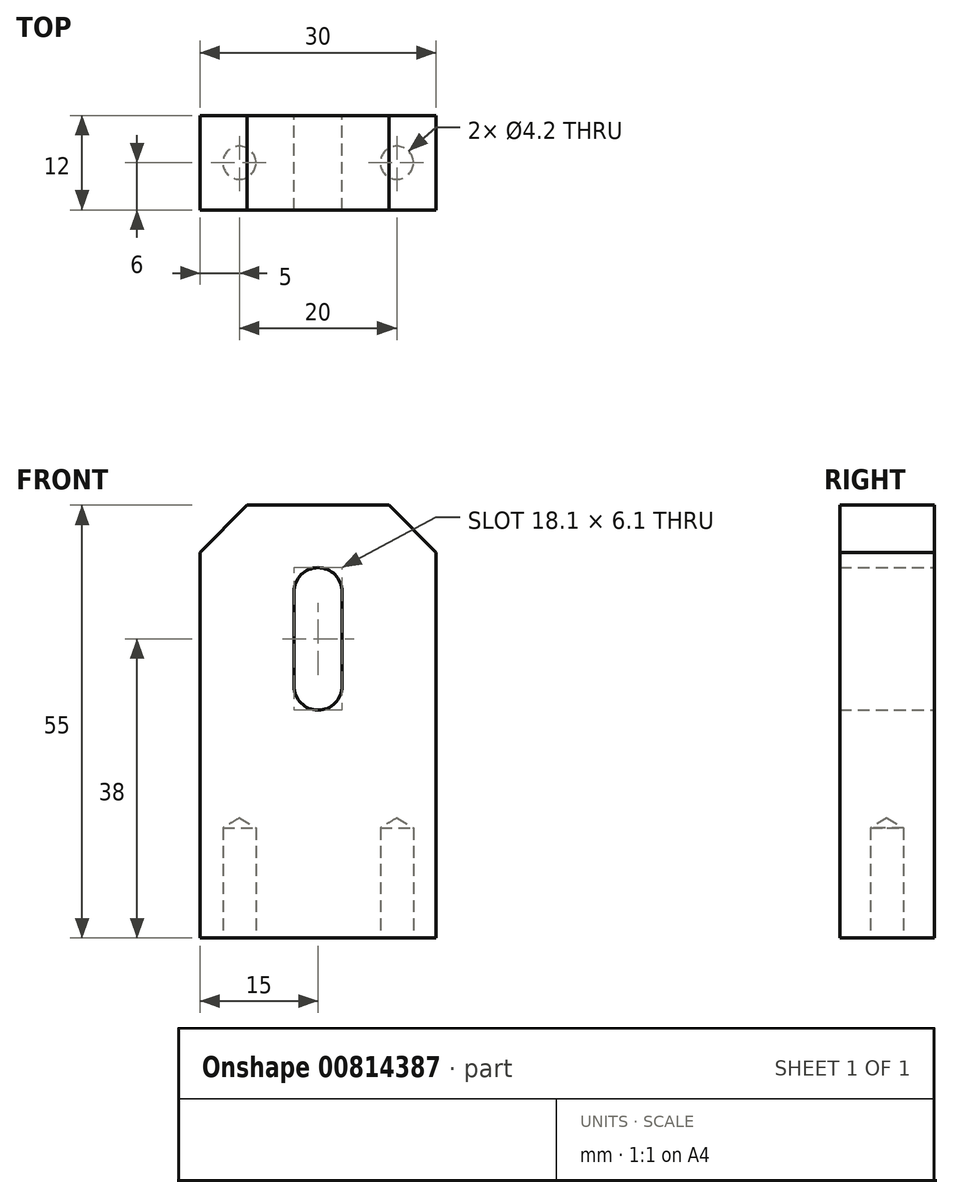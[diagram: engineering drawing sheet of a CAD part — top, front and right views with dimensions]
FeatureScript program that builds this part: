
annotation { "Feature Type Name" : "Feature", "Feature Type Description" : "" }
export const myFeature = defineFeature(function(context is Context, id is Id, definition is map)
    precondition{}
    {
        {
            var Q0;
            Q0=qCreatedBy(makeId("Front.planeOp"),FACE);
            var sketch = newSketch(context, id + "F0", { "sketchPlane" : qUnion([Q0])});
            skLineSegment(sketch, "E0.bottom", {"start": v(-15, -27.5) * mm, "end": v(15, -27.5) * mm});
            skLineSegment(sketch, "E0.top", {"start": v(-15, 27.5) * mm, "end": v(15, 27.5) * mm});
            skLineSegment(sketch, "E0.left", {"start": v(-15, -27.5) * mm, "end": v(-15, 27.5) * mm});
            skLineSegment(sketch, "E0.right", {"start": v(15, -27.5) * mm, "end": v(15, 27.5) * mm});
            skCircle(sketch, "E1", {"center": v(0, 16.5) * mm, "radius": 3.05 * mm});
            skPoint(sketch, "E2.center.orphan", {"position": v(0, 14.16) * mm});
            skCircle(sketch, "E3", {"center": v(0, 4.5) * mm, "radius": 3.05 * mm});
            skLineSegment(sketch, "E4", {"start": v(3.05, 16.5) * mm, "end": v(3.05, 4.5) * mm});
            skLineSegment(sketch, "E5", {"start": v(-3.05, 4.5) * mm, "end": v(-3.05, 16.5) * mm});
            skSolve(sketch);
        }
        {
            var Q0;
            Q0=makeQuery(id+"F0.imprint","IMPRINT",FACE,{"disambiguationData":[TD([[makeQuery(id+"F0.imprint","IMPRINT",EDGE,{"derivedFrom":sQuery(id+"F0.wireOp",EDGE,"E0.bottom")}),1.0]])]});
            extrude(context, id + "F1", {"entities" : qUnion([Q0]), "depth" : 12 * mm, "offsetDistance" : 25 * mm});
        }
        {
            var Q0;
            Q0=makeQuery(id+"F1.opExtrude","SWEPT_EDGE",EDGE,{"disambiguationData":[OSD([sQuery(id+"F0.wireOp",EDGE,"E0.top"),sQuery(id+"F0.wireOp",EDGE,"E0.left")])]});
            var Q1;
            Q1=makeQuery(id+"F1.opExtrude","SWEPT_EDGE",EDGE,{"disambiguationData":[OSD([sQuery(id+"F0.wireOp",EDGE,"E0.top"),sQuery(id+"F0.wireOp",EDGE,"E0.right")])]});
            chamfer(context, id + "F2", {"entities" : qUnion([Q0, Q1]), "width" : 6 * mm, "tangentPropagation" : true});
        }
        {
            var Q0;
            Q0=makeQuery(id+"F1.opExtrude","SWEPT_FACE",FACE,{"disambiguationData":[OSD([sQuery(id+"F0.wireOp",EDGE,"E0.bottom")])]});
            var sketch = newSketch(context, id + "F3", { "sketchPlane" : qUnion([Q0])});
            skLineSegment(sketch, "E6", {"start": v(-10, 12) * mm, "end": v(-10, 0) * mm});
            skLineSegment(sketch, "E7", {"start": v(10, 12) * mm, "end": v(10, 0) * mm});
            skPoint(sketch, "E8", {"position": v(-10, 6) * mm});
            skPoint(sketch, "E9", {"position": v(10, 6) * mm});
            skSolve(sketch);
        }
        {
            var Q0;
            Q0=sQuery(id+"F3.wireOp",VERTEX,"E8");
            var Q1;
            Q1=sQuery(id+"F3.wireOp",VERTEX,"E9");
            var Q2;
            Q2=makeQuery(id+"F1.opExtrude","SWEPT_BODY",BODY,{"disambiguationData":[OSD([sQuery(id+"F0.wireOp",EDGE,"E0.bottom"),sQuery(id+"F0.wireOp",EDGE,"E0.top"),sQuery(id+"F0.wireOp",EDGE,"E0.left"),sQuery(id+"F0.wireOp",EDGE,"E0.right"),sQuery(id+"F0.wireOp",EDGE,"E1"),sQuery(id+"F0.wireOp",EDGE,"E3"),sQuery(id+"F0.wireOp",EDGE,"E4"),sQuery(id+"F0.wireOp",EDGE,"E5")])]});
            hole(context, id + "F4", {"style" : HoleStyle.SIMPLE, "endStyle" : HoleEndStyle.BLIND, "holeDiameter" : 4.2 * mm, "majorDiameter" : 5 * mm, "holeDepth" : 14 * mm, "isTappedThrough" : true, "tappedDepth" : 12 * mm, "tapClearance" : 3, "locations" : qUnion([Q0, Q1]), "scope" : qUnion([Q2])});
        }
    });
